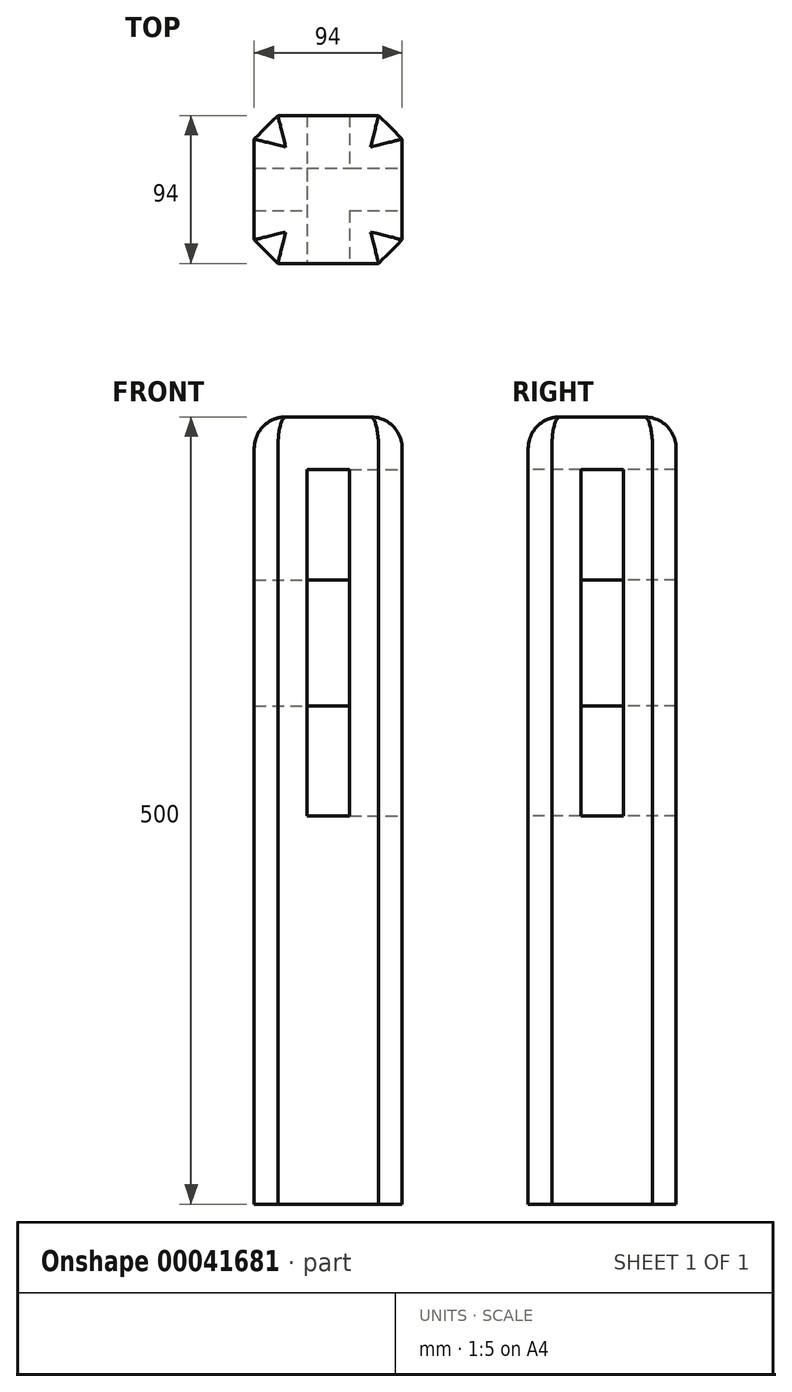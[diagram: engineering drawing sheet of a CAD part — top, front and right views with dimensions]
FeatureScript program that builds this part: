
annotation { "Feature Type Name" : "Feature", "Feature Type Description" : "" }
export const myFeature = defineFeature(function(context is Context, id is Id, definition is map)
    precondition{}
    {
        {
            var Q0;
            Q0=qCreatedBy(makeId("Top.planeOp"),FACE);
            var sketch = newSketch(context, id + "F0", { "sketchPlane" : qUnion([Q0])});
            skLineSegment(sketch, "E0.bottom", {"start": v(-47.13, 48) * mm, "end": v(46.87, 48) * mm});
            skLineSegment(sketch, "E0.top", {"start": v(-47.13, -46) * mm, "end": v(46.87, -46) * mm});
            skLineSegment(sketch, "E0.left", {"start": v(-47.13, 48) * mm, "end": v(-47.13, -46) * mm});
            skLineSegment(sketch, "E0.right", {"start": v(46.87, 48) * mm, "end": v(46.87, -46) * mm});
            skSolve(sketch);
        }
        {
            var Q0;
            Q0=makeQuery(id+"F0.imprint","IMPRINT",FACE,{"disambiguationData":[TD([[makeQuery(id+"F0.imprint","IMPRINT",EDGE,{"derivedFrom":sQuery(id+"F0.wireOp",EDGE,"E0.bottom")}),-1.0]])]});
            extrude(context, id + "F1", {"entities" : qUnion([Q0]), "depth" : 500 * mm});
        }
        {
            var Q0;
            Q0=makeQuery(id+"F1.opExtrude","SWEPT_FACE",FACE,{"disambiguationData":[OSD([sQuery(id+"F0.wireOp",EDGE,"E0.top")])]});
            var sketch = newSketch(context, id + "F2", { "sketchPlane" : qUnion([Q0])});
            skLineSegment(sketch, "E1.bottom", {"start": v(-13.63, 466.5) * mm, "end": v(13.37, 466.5) * mm});
            skLineSegment(sketch, "E1.top", {"start": v(-13.63, 246.5) * mm, "end": v(13.37, 246.5) * mm});
            skLineSegment(sketch, "E1.left", {"start": v(-13.63, 466.5) * mm, "end": v(-13.63, 246.5) * mm});
            skLineSegment(sketch, "E1.right", {"start": v(13.37, 466.5) * mm, "end": v(13.37, 246.5) * mm});
            skLineSegment(sketch, "E2.bottom", {"start": v(-13.63, 396.5) * mm, "end": v(13.37, 396.5) * mm});
            skLineSegment(sketch, "E2.top", {"start": v(-13.63, 316.5) * mm, "end": v(13.37, 316.5) * mm});
            skLineSegment(sketch, "E2.left", {"start": v(-13.63, 396.5) * mm, "end": v(-13.63, 316.5) * mm});
            skLineSegment(sketch, "E2.right", {"start": v(13.37, 396.5) * mm, "end": v(13.37, 316.5) * mm});
            skSolve(sketch);
        }
        {
            var Q0;
            Q0 = qSketchRegion(id + "F2", true);
            extrude(context, id + "F3", {"entities" : qUnion([Q0]), "operationType" : NewBodyOperationType.REMOVE, "oppositeDirection" : true, "depth" : 60.5 * mm});
        }
        {
            var Q0;
            Q0=makeQuery(id+"F1.opExtrude","SWEPT_FACE",FACE,{"disambiguationData":[OSD([sQuery(id+"F0.wireOp",EDGE,"E0.right")])]});
            var sketch = newSketch(context, id + "F4", { "sketchPlane" : qUnion([Q0])});
            skLineSegment(sketch, "E3.bottom", {"start": v(-12.5, 466.5) * mm, "end": v(14.5, 466.5) * mm});
            skLineSegment(sketch, "E3.top", {"start": v(-12.5, 246.5) * mm, "end": v(14.5, 246.5) * mm});
            skLineSegment(sketch, "E3.left", {"start": v(-12.5, 466.5) * mm, "end": v(-12.5, 246.5) * mm});
            skLineSegment(sketch, "E3.right", {"start": v(14.5, 466.5) * mm, "end": v(14.5, 246.5) * mm});
            skSolve(sketch);
        }
        {
            var Q0;
            Q0=makeQuery(id+"F4.imprint","IMPRINT",FACE,{"disambiguationData":[TD([[makeQuery(id+"F4.imprint","IMPRINT",EDGE,{"derivedFrom":sQuery(id+"F4.wireOp",EDGE,"E3.bottom")}),-1.0]])]});
            extrude(context, id + "F5", {"entities" : qUnion([Q0]), "operationType" : NewBodyOperationType.REMOVE, "oppositeDirection" : true, "depth" : 60.5 * mm});
        }
        {
            var Q0;
            Q0=makeQuery(id+"F1.opExtrude","SWEPT_FACE",FACE,{"disambiguationData":[OSD([sQuery(id+"F0.wireOp",EDGE,"E0.right")])]});
            var sketch = newSketch(context, id + "F6", { "sketchPlane" : qUnion([Q0])});
            skLineSegment(sketch, "E4.bottom", {"start": v(-12.5, 396.5) * mm, "end": v(14.5, 396.5) * mm});
            skLineSegment(sketch, "E4.top", {"start": v(-12.5, 316.5) * mm, "end": v(14.5, 316.5) * mm});
            skLineSegment(sketch, "E4.left", {"start": v(-12.5, 396.5) * mm, "end": v(-12.5, 316.5) * mm});
            skLineSegment(sketch, "E4.right", {"start": v(14.5, 396.5) * mm, "end": v(14.5, 316.5) * mm});
            skSolve(sketch);
        }
        {
            var Q0;
            Q0=makeQuery(id+"F6.imprint","IMPRINT",FACE,{"disambiguationData":[TD([[makeQuery(id+"F6.imprint","IMPRINT",EDGE,{"derivedFrom":sQuery(id+"F6.wireOp",EDGE,"E4.bottom")}),-1.0]])]});
            extrude(context, id + "F7", {"entities" : qUnion([Q0]), "operationType" : NewBodyOperationType.REMOVE, "oppositeDirection" : true, "depth" : 94 * mm});
        }
        {
            var Q0;
            Q0=makeQuery(id+"F1.opExtrude","SWEPT_FACE",FACE,{"disambiguationData":[OSD([sQuery(id+"F0.wireOp",EDGE,"E0.top")])]});
            var sketch = newSketch(context, id + "F8", { "sketchPlane" : qUnion([Q0])});
            skLineSegment(sketch, "E5.bottom", {"start": v(-13.63, 466.5) * mm, "end": v(13.37, 466.5) * mm});
            skLineSegment(sketch, "E5.top", {"start": v(-13.63, 396.5) * mm, "end": v(13.37, 396.5) * mm});
            skLineSegment(sketch, "E5.left", {"start": v(-13.63, 466.5) * mm, "end": v(-13.63, 396.5) * mm});
            skLineSegment(sketch, "E5.right", {"start": v(13.37, 466.5) * mm, "end": v(13.37, 396.5) * mm});
            skLineSegment(sketch, "E6.bottom", {"start": v(-13.63, 246.5) * mm, "end": v(13.37, 246.5) * mm});
            skLineSegment(sketch, "E6.top", {"start": v(-13.63, 316.5) * mm, "end": v(13.37, 316.5) * mm});
            skLineSegment(sketch, "E6.left", {"start": v(-13.63, 246.5) * mm, "end": v(-13.63, 316.5) * mm});
            skLineSegment(sketch, "E6.right", {"start": v(13.37, 246.5) * mm, "end": v(13.37, 316.5) * mm});
            skSolve(sketch);
        }
        {
            var Q0;
            Q0=makeQuery(id+"F8.imprint","IMPRINT",FACE,{"disambiguationData":[TD([[makeQuery(id+"F8.imprint","IMPRINT",EDGE,{"derivedFrom":sQuery(id+"F8.wireOp",EDGE,"E5.bottom")}),-1.0]])]});
            var Q1;
            Q1=makeQuery(id+"F8.imprint","IMPRINT",FACE,{"disambiguationData":[TD([[makeQuery(id+"F8.imprint","IMPRINT",EDGE,{"derivedFrom":sQuery(id+"F8.wireOp",EDGE,"E6.bottom")}),1.0]])]});
            extrude(context, id + "F9", {"entities" : qUnion([Q0, Q1]), "operationType" : NewBodyOperationType.REMOVE, "oppositeDirection" : true, "depth" : 94 * mm});
        }
        {
            var Q0;
            Q0=makeQuery(id+"F1.opExtrude","CAP_EDGE",EDGE,{"disambiguationData":[OSD([sQuery(id+"F0.wireOp",EDGE,"E0.top")])],"isStart":false});
            var Q1;
            Q1=makeQuery(id+"F1.opExtrude","CAP_EDGE",EDGE,{"disambiguationData":[OSD([sQuery(id+"F0.wireOp",EDGE,"E0.right")])],"isStart":false});
            var Q2;
            Q2=makeQuery(id+"F1.opExtrude","CAP_EDGE",EDGE,{"disambiguationData":[OSD([sQuery(id+"F0.wireOp",EDGE,"E0.bottom")])],"isStart":false});
            var Q3;
            Q3=makeQuery(id+"F1.opExtrude","CAP_EDGE",EDGE,{"disambiguationData":[OSD([sQuery(id+"F0.wireOp",EDGE,"E0.left")])],"isStart":false});
            fillet(context, id + "F10", {"entities" : qUnion([Q0, Q1, Q2, Q3]), "radius" : 20 * mm, "tangentPropagation" : true, "allowEdgeOverflow" : false});
        }
        {
            var Q0;
            Q0=makeQuery(id+"F1.opExtrude","SWEPT_EDGE",EDGE,{"disambiguationData":[OSD([sQuery(id+"F0.wireOp",EDGE,"E0.top"),sQuery(id+"F0.wireOp",EDGE,"E0.right")])]});
            var Q1;
            Q1=makeQuery(id+"F1.opExtrude","SWEPT_EDGE",EDGE,{"disambiguationData":[OSD([sQuery(id+"F0.wireOp",EDGE,"E0.bottom"),sQuery(id+"F0.wireOp",EDGE,"E0.right")])]});
            var Q2;
            Q2=makeQuery(id+"F1.opExtrude","SWEPT_EDGE",EDGE,{"disambiguationData":[OSD([sQuery(id+"F0.wireOp",EDGE,"E0.bottom"),sQuery(id+"F0.wireOp",EDGE,"E0.left")])]});
            var Q3;
            Q3=makeQuery(id+"F1.opExtrude","SWEPT_EDGE",EDGE,{"disambiguationData":[OSD([sQuery(id+"F0.wireOp",EDGE,"E0.top"),sQuery(id+"F0.wireOp",EDGE,"E0.left")])]});
            chamfer(context, id + "F11", {"entities" : qUnion([Q0, Q1, Q2, Q3]), "width" : 15 * mm, "tangentPropagation" : true});
        }
    });
